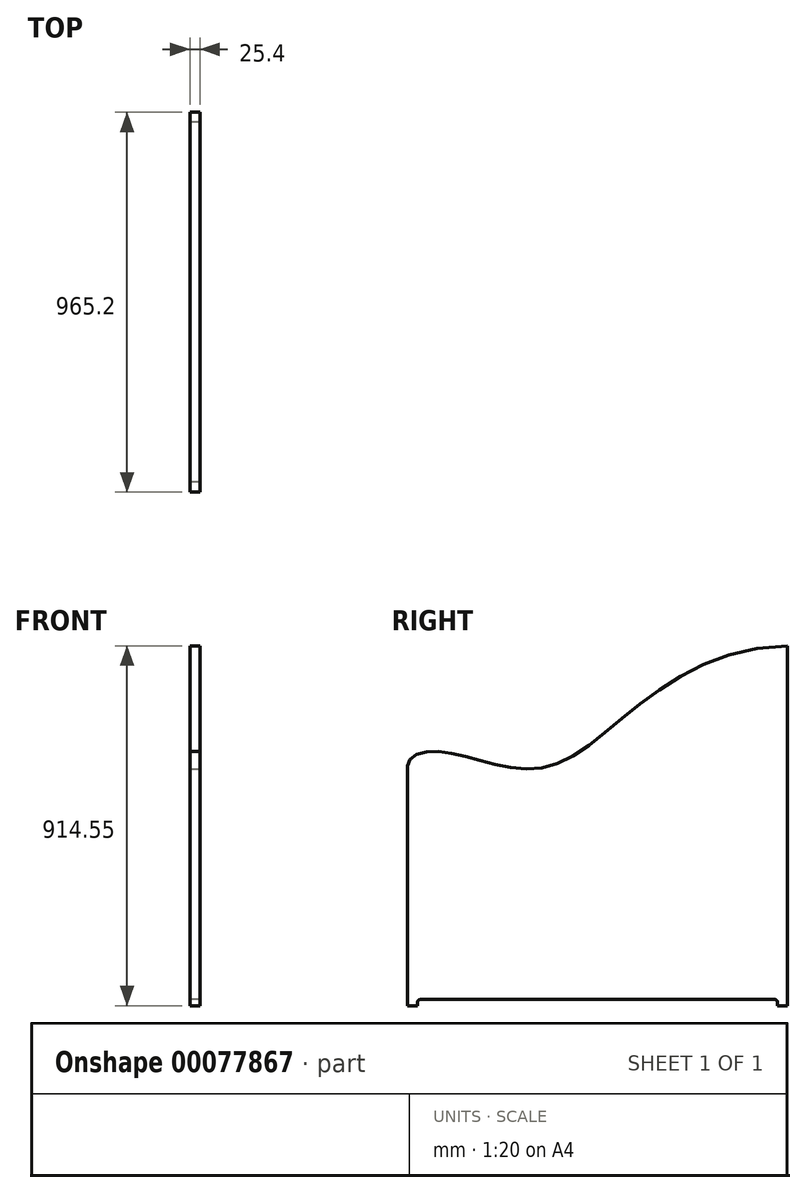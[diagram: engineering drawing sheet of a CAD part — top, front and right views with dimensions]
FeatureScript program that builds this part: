
annotation { "Feature Type Name" : "Feature", "Feature Type Description" : "" }
export const myFeature = defineFeature(function(context is Context, id is Id, definition is map)
    precondition{}
    {
        {
            var Q0;
            Q0=qCreatedBy(makeId("Right.planeOp"),FACE);
            var sketch = newSketch(context, id + "F0", { "sketchPlane" : qUnion([Q0])});
            skLineSegment(sketch, "E0", {"start": v(-60.3, 564.69) * mm, "end": v(-60.3, -44.91) * mm});
            skLineSegment(sketch, "E1", {"start": v(-60.3, -44.91) * mm, "end": v(-34.9, -44.91) * mm});
            skLineSegment(sketch, "E2", {"start": v(-34.9, -44.91) * mm, "end": v(-34.9, -35.84) * mm});
            skLineSegment(sketch, "E3", {"start": v(-28.55, -29.49) * mm, "end": v(873.15, -29.49) * mm});
            skLineSegment(sketch, "E4", {"start": v(879.5, -35.84) * mm, "end": v(879.5, -44.76) * mm});
            skLineSegment(sketch, "E5", {"start": v(879.5, -44.76) * mm, "end": v(904.9, -44.76) * mm});
            skLineSegment(sketch, "E6", {"start": v(904.9, -44.76) * mm, "end": v(904.9, 869.64) * mm});
            skFitSpline(sketch, "E7", {"points": [v(-60.3, 564.69) * mm, v(24.96, 600.14) * mm, v(305.4, 564.69) * mm, v(904.9, 869.64) * mm], "startDerivative": vector(4.32, 434.58) * mm, "endDerivative": vector(1891, 29.25) * mm});
            skPoint(sketch, "E8.visualSharp", {"position": v(-34.9, -29.49) * mm});
            skArc(sketch, "E8.filletArc", {"start": v(-28.55, -29.49) * mm, "mid": v(-33.04, -31.35) * mm, "end": v(-34.9, -35.84) * mm});
            skPoint(sketch, "E9.visualSharp", {"position": v(879.5, -29.49) * mm});
            skArc(sketch, "E9.filletArc", {"start": v(879.5, -35.84) * mm, "mid": v(877.64, -31.35) * mm, "end": v(873.15, -29.49) * mm});
            skLineSegment(sketch, "E10", {"start": v(-34.9, -44.91) * mm, "end": v(879.5, -44.76) * mm, "construction": true});
            skSolve(sketch);
        }
        {
            var Q0;
            Q0 = qSketchRegion(id + "F0", true);
            extrude(context, id + "F1", {"entities" : qUnion([Q0]), "depth" : 25.4 * mm});
        }
    });
